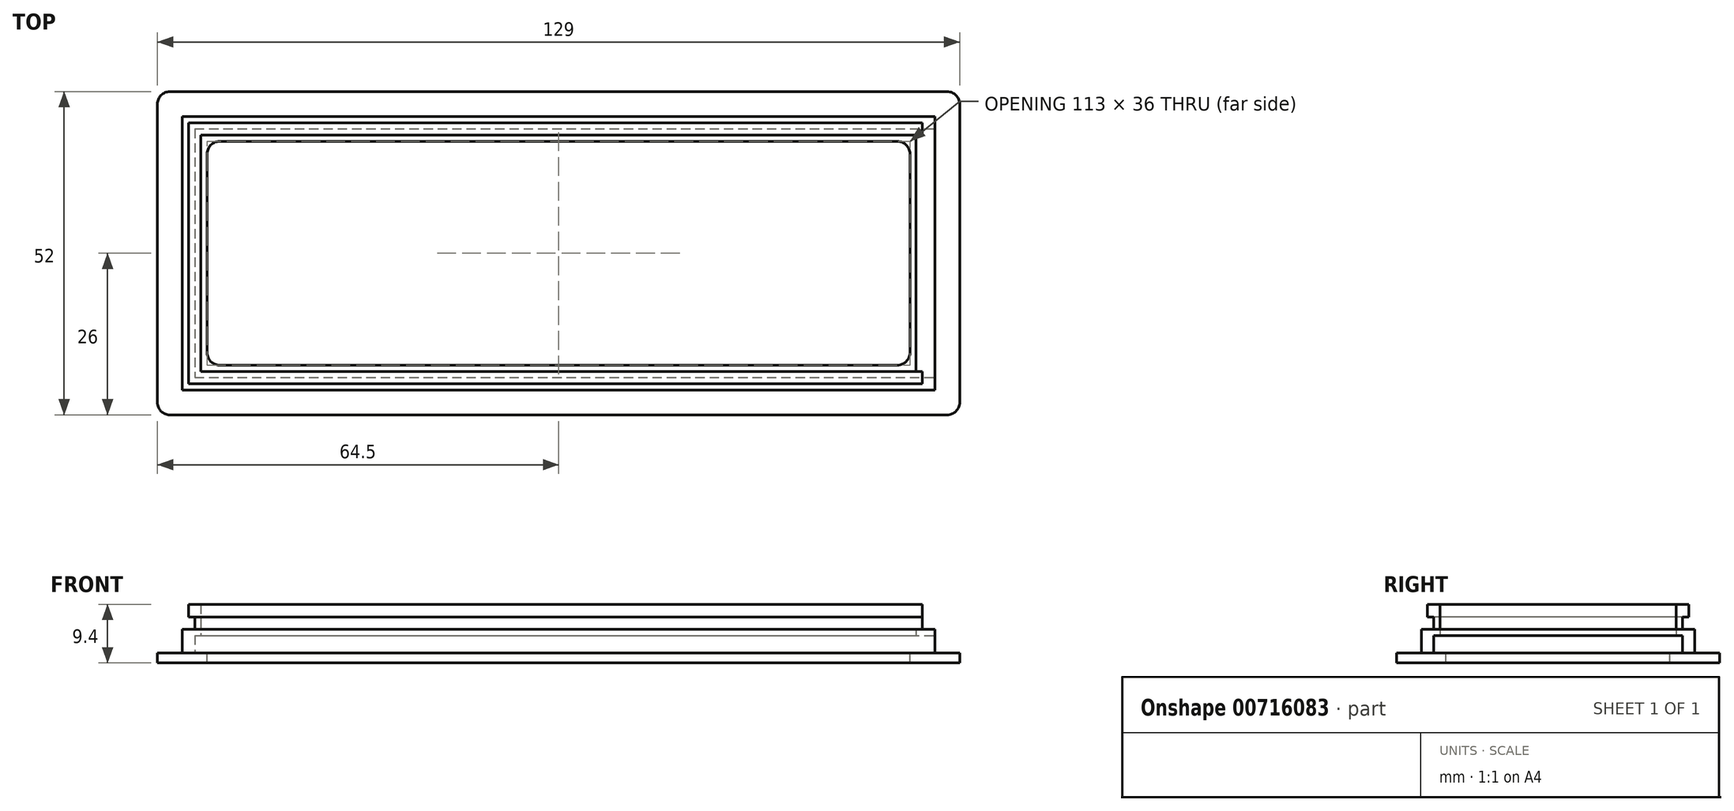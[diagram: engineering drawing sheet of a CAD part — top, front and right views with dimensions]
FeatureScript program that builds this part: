
annotation { "Feature Type Name" : "Feature", "Feature Type Description" : "" }
export const myFeature = defineFeature(function(context is Context, id is Id, definition is map)
    precondition{}
    {
        {
            var Q0;
            Q0=qCreatedBy(makeId("Top.planeOp"),FACE);
            var sketch = newSketch(context, id + "F0", { "sketchPlane" : qUnion([Q0])});
            skLineSegment(sketch, "E0.bottom", {"start": v(-58.5, 20) * mm, "end": v(60.5, 20) * mm});
            skLineSegment(sketch, "E0.top", {"start": v(-58.5, -20) * mm, "end": v(60.5, -20) * mm});
            skLineSegment(sketch, "E0.left", {"start": v(-58.5, 20) * mm, "end": v(-58.5, -20) * mm});
            skLineSegment(sketch, "E0.right", {"start": v(58.5, 20) * mm, "end": v(58.5, -20) * mm});
            skPoint(sketch, "E0.middle", {"position": v(0, 0) * mm});
            skLineSegment(sketch, "E1.bottom", {"start": v(-54.5, 18) * mm, "end": v(54.5, 18) * mm});
            skLineSegment(sketch, "E1.top", {"start": v(-54.5, -18) * mm, "end": v(54.5, -18) * mm});
            skLineSegment(sketch, "E1.left", {"start": v(-56.5, 16) * mm, "end": v(-56.5, -16) * mm});
            skLineSegment(sketch, "E1.right", {"start": v(56.5, 16) * mm, "end": v(56.5, -16) * mm});
            skLineSegment(sketch, "E2.bottom", {"start": v(-62.5, 26) * mm, "end": v(62.5, 26) * mm});
            skLineSegment(sketch, "E2.top", {"start": v(-62.5, -26) * mm, "end": v(62.5, -26) * mm});
            skLineSegment(sketch, "E2.left", {"start": v(-64.5, 24) * mm, "end": v(-64.5, -24) * mm});
            skLineSegment(sketch, "E2.right", {"start": v(64.5, 24) * mm, "end": v(64.5, -24) * mm});
            skPoint(sketch, "E3.visualSharp", {"position": v(-64.5, 26) * mm});
            skArc(sketch, "E3.filletArc", {"start": v(-62.5, 26) * mm, "mid": v(-63.91, 25.41) * mm, "end": v(-64.5, 24) * mm});
            skPoint(sketch, "E4.visualSharp", {"position": v(-64.5, -26) * mm});
            skArc(sketch, "E4.filletArc", {"start": v(-64.5, -24) * mm, "mid": v(-63.91, -25.41) * mm, "end": v(-62.5, -26) * mm});
            skPoint(sketch, "E5.visualSharp", {"position": v(64.5, -26) * mm});
            skArc(sketch, "E5.filletArc", {"start": v(62.5, -26) * mm, "mid": v(63.91, -25.41) * mm, "end": v(64.5, -24) * mm});
            skPoint(sketch, "E6.visualSharp", {"position": v(64.5, 26) * mm});
            skArc(sketch, "E6.filletArc", {"start": v(64.5, 24) * mm, "mid": v(63.91, 25.41) * mm, "end": v(62.5, 26) * mm});
            skPoint(sketch, "E7.visualSharp", {"position": v(56.5, 18) * mm});
            skArc(sketch, "E7.filletArc", {"start": v(56.5, 16) * mm, "mid": v(55.91, 17.41) * mm, "end": v(54.5, 18) * mm});
            skPoint(sketch, "E8.visualSharp", {"position": v(-56.5, 18) * mm});
            skArc(sketch, "E8.filletArc", {"start": v(-54.5, 18) * mm, "mid": v(-55.91, 17.41) * mm, "end": v(-56.5, 16) * mm});
            skPoint(sketch, "E9.visualSharp", {"position": v(-56.5, -18) * mm});
            skArc(sketch, "E9.filletArc", {"start": v(-56.5, -16) * mm, "mid": v(-55.91, -17.41) * mm, "end": v(-54.5, -18) * mm});
            skPoint(sketch, "E10.visualSharp", {"position": v(56.5, -18) * mm});
            skArc(sketch, "E10.filletArc", {"start": v(54.5, -18) * mm, "mid": v(55.91, -17.41) * mm, "end": v(56.5, -16) * mm});
            skLineSegment(sketch, "E11.bottom", {"start": v(-60.5, 22) * mm, "end": v(60.5, 22) * mm});
            skLineSegment(sketch, "E11.top", {"start": v(-60.5, -22) * mm, "end": v(60.5, -22) * mm});
            skLineSegment(sketch, "E11.left", {"start": v(-60.5, 22) * mm, "end": v(-60.5, -22) * mm});
            skLineSegment(sketch, "E11.right", {"start": v(60.5, 22) * mm, "end": v(60.5, -22) * mm});
            skSolve(sketch);
        }
        {
            var Q0;
            Q0=makeQuery(id+"F0.imprint","IMPRINT",FACE,{"disambiguationData":[TD([[makeQuery(id+"F0.imprint","IMPRINT",EDGE,{"derivedFrom":sQuery(id+"F0.wireOp",EDGE,"E2.bottom")}),-1.0]])]});
            var Q1;
            {var subQ8=sQuery(id+"F0.wireOp",EDGE,"E0.left");Q1=makeQuery(id+"F0.imprint","IMPRINT",FACE,{"disambiguationData":[TD([[makeQuery(id+"F0.imprint","IMPRINT",EDGE,{"derivedFrom":subQ8}),-1.0]])]});}
            var Q2;
            {var subQ0=sQuery(id+"F0.wireOp",EDGE,"E0.left");Q2=makeQuery(id+"F0.imprint","IMPRINT",FACE,{"disambiguationData":[TD([[makeQuery(id+"F0.imprint","IMPRINT",EDGE,{"derivedFrom":subQ0}),1.0]])]});}
            var Q3;
            {var subQ3=sQuery(id+"F0.wireOp",EDGE,"E0.right");Q3=makeQuery(id+"F0.imprint","IMPRINT",FACE,{"disambiguationData":[TD([[makeQuery(id+"F0.imprint","IMPRINT",EDGE,{"derivedFrom":subQ3}),1.0]])]});}
            extrude(context, id + "F1", {"entities" : qUnion([Q0, Q1, Q2, Q3]), "oppositeDirection" : true, "depth" : 1.6 * mm, "offsetDistance" : 25 * mm});
        }
        {
            var Q0;
            {var subQ8=sQuery(id+"F0.wireOp",EDGE,"E0.left");Q0=makeQuery(id+"F0.imprint","IMPRINT",FACE,{"disambiguationData":[TD([[makeQuery(id+"F0.imprint","IMPRINT",EDGE,{"derivedFrom":subQ8}),-1.0]])]});}
            extrude(context, id + "F2", {"entities" : qUnion([Q0]), "operationType" : NewBodyOperationType.ADD, "depth" : 2.8 * mm, "offsetDistance" : 25 * mm});
        }
        {
            var Q0;
            Q0=makeQuery(id+"F2.opExtrude","CAP_FACE",FACE,{"disambiguationData":[OSD([sQuery(id+"F0.wireOp",EDGE,"E0.bottom"),sQuery(id+"F0.wireOp",EDGE,"E0.top"),sQuery(id+"F0.wireOp",EDGE,"E0.left"),sQuery(id+"F0.wireOp",EDGE,"E11.bottom"),sQuery(id+"F0.wireOp",EDGE,"E11.top"),sQuery(id+"F0.wireOp",EDGE,"E11.left"),sQuery(id+"F0.wireOp",EDGE,"E11.right")])],"isStart":false});
            var sketch = newSketch(context, id + "F3", { "sketchPlane" : qUnion([Q0])});
            skLineSegment(sketch, "E12.bottom", {"start": v(-60.5, 22) * mm, "end": v(60.5, 22) * mm});
            skLineSegment(sketch, "E12.top", {"start": v(-60.5, -22) * mm, "end": v(60.5, -22) * mm});
            skLineSegment(sketch, "E12.left", {"start": v(-60.5, 22) * mm, "end": v(-60.5, -22) * mm});
            skLineSegment(sketch, "E12.right", {"start": v(60.5, 22) * mm, "end": v(60.5, -22) * mm});
            skPoint(sketch, "E12.middle", {"position": v(0, 0) * mm});
            skLineSegment(sketch, "E13.bottom", {"start": v(-57.5, 19) * mm, "end": v(57.5, 19) * mm});
            skLineSegment(sketch, "E13.top", {"start": v(-57.5, -19) * mm, "end": v(57.5, -19) * mm});
            skLineSegment(sketch, "E13.left", {"start": v(-57.5, 19) * mm, "end": v(-57.5, -19) * mm});
            skLineSegment(sketch, "E13.right", {"start": v(57.5, 19) * mm, "end": v(57.5, -19) * mm});
            skSolve(sketch);
        }
        {
            var Q0;
            {var subQ2=sQuery(id+"F3.wireOp",EDGE,"E12.bottom");Q0=makeQuery(id+"F3.imprint","IMPRINT",FACE,{"disambiguationData":[TD([[makeQuery(id+"F3.imprint","IMPRINT",EDGE,{"derivedFrom":subQ2}),-1.0]])]});}
            var Q1;
            Q1=makeQuery(id+"F3.imprint","IMPRINT",FACE,{"disambiguationData":[TD([[makeQuery(id+"F3.imprint","IMPRINT",EDGE,{"derivedFrom":sQuery(id+"F3.wireOp",EDGE,"E13.bottom")}),1.0]])]});
            extrude(context, id + "F4", {"entities" : qUnion([Q0, Q1]), "operationType" : NewBodyOperationType.ADD, "depth" : 1 * mm, "offsetDistance" : 25 * mm});
        }
        {
            var Q0;
            Q0=makeQuery(id+"F4.opExtrude","CAP_FACE",FACE,{"disambiguationData":[OSD([sQuery(id+"F3.wireOp",EDGE,"E12.bottom"),sQuery(id+"F3.wireOp",EDGE,"E12.top"),sQuery(id+"F3.wireOp",EDGE,"E12.left"),sQuery(id+"F3.wireOp",EDGE,"E12.right"),sQuery(id+"F3.wireOp",EDGE,"E13.bottom"),sQuery(id+"F3.wireOp",EDGE,"E13.top"),sQuery(id+"F3.wireOp",EDGE,"E13.left"),sQuery(id+"F3.wireOp",EDGE,"E13.right")])],"isStart":false});
            var sketch = newSketch(context, id + "F5", { "sketchPlane" : qUnion([Q0])});
            skLineSegment(sketch, "E14.bottom", {"start": v(-57.5, 19) * mm, "end": v(58.5, 19) * mm});
            skLineSegment(sketch, "E14.top", {"start": v(-57.5, -19) * mm, "end": v(58.5, -19) * mm});
            skLineSegment(sketch, "E14.left", {"start": v(-57.5, 19) * mm, "end": v(-57.5, -19) * mm});
            skLineSegment(sketch, "E14.right", {"start": v(57.5, 19) * mm, "end": v(57.5, -19) * mm});
            skPoint(sketch, "E14.middle", {"position": v(0, 0) * mm});
            skLineSegment(sketch, "E15.bottom", {"start": v(-58.5, 20) * mm, "end": v(58.5, 20) * mm});
            skLineSegment(sketch, "E15.top", {"start": v(-58.5, -20) * mm, "end": v(58.5, -20) * mm});
            skLineSegment(sketch, "E15.left", {"start": v(-58.5, 20) * mm, "end": v(-58.5, -20) * mm});
            skLineSegment(sketch, "E15.right", {"start": v(58.5, 20) * mm, "end": v(58.5, -20) * mm});
            skSolve(sketch);
        }
        {
            var Q0;
            Q0=makeQuery(id+"F5.imprint","IMPRINT",FACE,{"disambiguationData":[TD([[makeQuery(id+"F5.imprint","IMPRINT",EDGE,{"derivedFrom":sQuery(id+"F5.wireOp",EDGE,"E14.bottom")}),1.0]])]});
            extrude(context, id + "F6", {"entities" : qUnion([Q0]), "operationType" : NewBodyOperationType.ADD, "depth" : 2 * mm, "offsetDistance" : 25 * mm});
        }
        {
            var Q0;
            Q0=makeQuery(id+"F6.opExtrude","CAP_FACE",FACE,{"disambiguationData":[OSD([sQuery(id+"F5.wireOp",EDGE,"E14.bottom"),sQuery(id+"F5.wireOp",EDGE,"E14.top"),sQuery(id+"F5.wireOp",EDGE,"E14.left"),sQuery(id+"F5.wireOp",EDGE,"E15.bottom"),sQuery(id+"F5.wireOp",EDGE,"E15.top"),sQuery(id+"F5.wireOp",EDGE,"E15.left"),sQuery(id+"F5.wireOp",EDGE,"E15.right")])],"isStart":false});
            var sketch = newSketch(context, id + "F7", { "sketchPlane" : qUnion([Q0])});
            skLineSegment(sketch, "E16.bottom", {"start": v(-57.5, 19) * mm, "end": v(58.5, 19) * mm});
            skLineSegment(sketch, "E16.top", {"start": v(-57.5, -19) * mm, "end": v(58.5, -19) * mm});
            skLineSegment(sketch, "E16.left", {"start": v(-57.5, 19) * mm, "end": v(-57.5, -19) * mm});
            skLineSegment(sketch, "E16.right", {"start": v(57.5, 19) * mm, "end": v(57.5, -19) * mm});
            skPoint(sketch, "E16.middle", {"position": v(0, 0) * mm});
            skLineSegment(sketch, "E17.bottom", {"start": v(-59.5, 21) * mm, "end": v(59.5, 21) * mm});
            skLineSegment(sketch, "E17.top", {"start": v(-59.5, -21) * mm, "end": v(59.5, -21) * mm});
            skLineSegment(sketch, "E17.left", {"start": v(-59.5, 21) * mm, "end": v(-59.5, -21) * mm});
            skLineSegment(sketch, "E17.right", {"start": v(59.5, 21) * mm, "end": v(59.5, -21) * mm});
            skLineSegment(sketch, "E18", {"start": v(58.5, 19) * mm, "end": v(58.5, 21) * mm});
            skLineSegment(sketch, "E19", {"start": v(58.5, -19) * mm, "end": v(58.5, -21) * mm});
            skSolve(sketch);
        }
        {
            var Q0;
            {var subQ0=sQuery(id+"F7.wireOp",EDGE,"E17.left");Q0=makeQuery(id+"F7.imprint","IMPRINT",FACE,{"disambiguationData":[TD([[makeQuery(id+"F7.imprint","IMPRINT",EDGE,{"derivedFrom":subQ0}),1.0]])]});}
            var Q1;
            {var subQ5=sQuery(id+"F7.wireOp",EDGE,"E16.left");Q1=makeQuery(id+"F7.imprint","IMPRINT",FACE,{"disambiguationData":[TD([[makeQuery(id+"F7.imprint","IMPRINT",EDGE,{"derivedFrom":subQ5}),-1.0]])]});}
            extrude(context, id + "F8", {"entities" : qUnion([Q0, Q1]), "operationType" : NewBodyOperationType.ADD, "depth" : 2 * mm, "offsetDistance" : 25 * mm});
        }
    });
